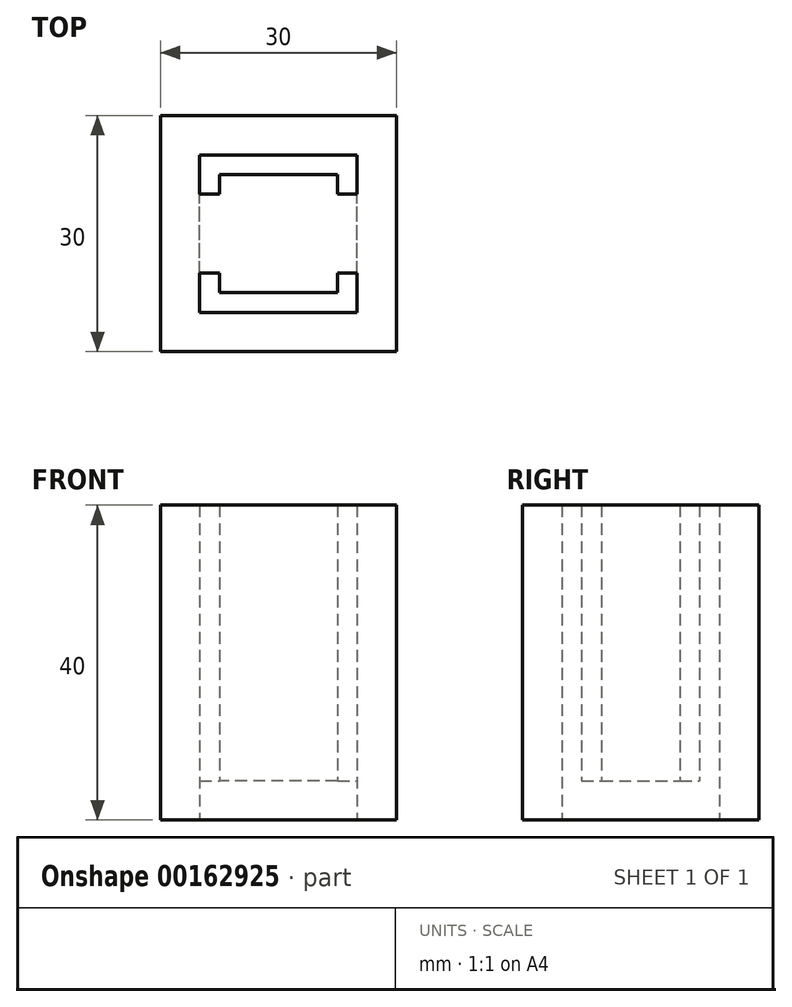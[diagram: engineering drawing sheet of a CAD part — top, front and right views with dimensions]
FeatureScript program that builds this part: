
annotation { "Feature Type Name" : "Feature", "Feature Type Description" : "" }
export const myFeature = defineFeature(function(context is Context, id is Id, definition is map)
    precondition{}
    {
        {
            var Q0;
            Q0=qCreatedBy(makeId("Top.planeOp"),FACE);
            var sketch = newSketch(context, id + "F0", { "sketchPlane" : qUnion([Q0])});
            skLineSegment(sketch, "E0.bottom", {"start": v(7.5, -7.5) * mm, "end": v(-7.5, -7.5) * mm});
            skLineSegment(sketch, "E0.top", {"start": v(7.5, 7.5) * mm, "end": v(-7.5, 7.5) * mm});
            skLineSegment(sketch, "E0.left", {"start": v(7.5, -7.5) * mm, "end": v(7.5, 7.5) * mm});
            skLineSegment(sketch, "E0.right", {"start": v(-7.5, -7.5) * mm, "end": v(-7.5, 7.5) * mm});
            skPoint(sketch, "E0.middle", {"position": v(0, 0) * mm});
            skLineSegment(sketch, "E1.bottom", {"start": v(10, -10) * mm, "end": v(-10, -10) * mm});
            skLineSegment(sketch, "E1.top", {"start": v(10, 10) * mm, "end": v(-10, 10) * mm});
            skLineSegment(sketch, "E1.left", {"start": v(10, -10) * mm, "end": v(10, 10) * mm});
            skLineSegment(sketch, "E1.right", {"start": v(-10, -10) * mm, "end": v(-10, 10) * mm});
            skLineSegment(sketch, "E2.bottom", {"start": v(-15, 15) * mm, "end": v(15, 15) * mm});
            skLineSegment(sketch, "E2.top", {"start": v(-15, -15) * mm, "end": v(15, -15) * mm});
            skLineSegment(sketch, "E2.left", {"start": v(-15, 15) * mm, "end": v(-15, -15) * mm});
            skLineSegment(sketch, "E2.right", {"start": v(15, 15) * mm, "end": v(15, -15) * mm});
            skLineSegment(sketch, "E3", {"start": v(-10, 5) * mm, "end": v(10, 5) * mm});
            skLineSegment(sketch, "E4", {"start": v(-7.5, 0) * mm, "end": v(7.5, 0) * mm, "construction": true});
            skLineSegment(sketch, "E5.MirrorCS", {"start": v(-10, -5) * mm, "end": v(10, -5) * mm});
            skSolve(sketch);
        }
        {
            var Q0;
            {var subQ0=sQuery(id+"F0.wireOp",EDGE,"E0.top");Q0=makeQuery(id+"F0.imprint","IMPRINT",FACE,{"disambiguationData":[TD([[makeQuery(id+"F0.imprint","IMPRINT",EDGE,{"derivedFrom":subQ0}),1.0]])]});}
            var Q1;
            {var subQ0=sQuery(id+"F0.wireOp",EDGE,"E5.MirrorCS");var subQ1=sQuery(id+"F0.wireOp",EDGE,"E0.left");var subQ2=makeQuery(id+"F0.imprint","INTERSECT",VERTEX,{"derivedFrom":[subQ1,subQ0]});Q1=makeQuery(id+"F0.imprint","IMPRINT",FACE,{"disambiguationData":[TD([[makeQuery(id+"F0.imprint","IMPRINT",EDGE,{"disambiguationData":[TD([[subQ2,-1.0]])],"derivedFrom":subQ1}),1.0]])]});}
            var Q2;
            {var subQ0=sQuery(id+"F0.wireOp",EDGE,"E0.bottom");Q2=makeQuery(id+"F0.imprint","IMPRINT",FACE,{"disambiguationData":[TD([[makeQuery(id+"F0.imprint","IMPRINT",EDGE,{"derivedFrom":subQ0}),-1.0]])]});}
            var Q3;
            {var subQ0=sQuery(id+"F0.wireOp",EDGE,"E5.MirrorCS");var subQ1=sQuery(id+"F0.wireOp",EDGE,"E0.left");var subQ2=makeQuery(id+"F0.imprint","INTERSECT",VERTEX,{"derivedFrom":[subQ1,subQ0]});Q3=makeQuery(id+"F0.imprint","IMPRINT",FACE,{"disambiguationData":[TD([[makeQuery(id+"F0.imprint","IMPRINT",EDGE,{"disambiguationData":[TD([[subQ2,-1.0]])],"derivedFrom":subQ1}),-1.0]])]});}
            var Q4;
            {var subQ7=sQuery(id+"F0.wireOp",EDGE,"E0.top");Q4=makeQuery(id+"F0.imprint","IMPRINT",FACE,{"disambiguationData":[TD([[makeQuery(id+"F0.imprint","IMPRINT",EDGE,{"derivedFrom":subQ7}),-1.0]])]});}
            var Q5;
            {var subQ0=sQuery(id+"F0.wireOp",EDGE,"E5.MirrorCS");var subQ1=sQuery(id+"F0.wireOp",EDGE,"E0.right");var subQ2=makeQuery(id+"F0.imprint","INTERSECT",VERTEX,{"derivedFrom":[subQ1,subQ0]});Q5=makeQuery(id+"F0.imprint","IMPRINT",FACE,{"disambiguationData":[TD([[makeQuery(id+"F0.imprint","IMPRINT",EDGE,{"disambiguationData":[TD([[subQ2,-1.0]])],"derivedFrom":subQ1}),1.0]])]});}
            var Q6;
            {var subQ2=sQuery(id+"F0.wireOp",EDGE,"E0.bottom");Q6=makeQuery(id+"F0.imprint","IMPRINT",FACE,{"disambiguationData":[TD([[makeQuery(id+"F0.imprint","IMPRINT",EDGE,{"derivedFrom":subQ2}),1.0]])]});}
            var Q7;
            {var subQ4=sQuery(id+"F0.wireOp",EDGE,"E1.bottom");Q7=makeQuery(id+"F0.imprint","IMPRINT",FACE,{"disambiguationData":[TD([[makeQuery(id+"F0.imprint","IMPRINT",EDGE,{"derivedFrom":subQ4}),1.0]])]});}
            var Q8;
            Q8=makeQuery(id+"F2.opExtrude","SWEPT_BODY",BODY,{"disambiguationData":[OSD([sQuery(id+"F0.wireOp",EDGE,"E0.bottom"),sQuery(id+"F0.wireOp",EDGE,"E0.top"),sQuery(id+"F0.wireOp",EDGE,"E0.left"),sQuery(id+"F0.wireOp",EDGE,"E0.right"),sQuery(id+"F0.wireOp",EDGE,"E1.left"),sQuery(id+"F0.wireOp",EDGE,"SQ9eBi6W-tF5L-iBfu-zbn4-8iLzbDoy28uW"),sQuery(id+"F0.wireOp",EDGE,"c3725698-1aea-4c50-8bbd-dbaeecdf150d0.MirrorCS")])]});
            extrude(context, id + "F1", {"entities" : qUnion([Q0, Q1, Q2, Q3, Q4, Q5, Q6, Q7]), "endBoundEntityBody" : qUnion([Q8]), "depth" : 40 * mm});
        }
        {
            var Q0;
            {var subQ0=sQuery(id+"F0.wireOp",EDGE,"E0.bottom");Q0=makeQuery(id+"F0.imprint","IMPRINT",FACE,{"disambiguationData":[TD([[makeQuery(id+"F0.imprint","IMPRINT",EDGE,{"derivedFrom":subQ0}),-1.0]])]});}
            var Q1;
            {var subQ0=sQuery(id+"F0.wireOp",EDGE,"E5.MirrorCS");var subQ1=sQuery(id+"F0.wireOp",EDGE,"E0.left");var subQ2=makeQuery(id+"F0.imprint","INTERSECT",VERTEX,{"derivedFrom":[subQ1,subQ0]});Q1=makeQuery(id+"F0.imprint","IMPRINT",FACE,{"disambiguationData":[TD([[makeQuery(id+"F0.imprint","IMPRINT",EDGE,{"disambiguationData":[TD([[subQ2,-1.0]])],"derivedFrom":subQ1}),1.0]])]});}
            var Q2;
            {var subQ0=sQuery(id+"F0.wireOp",EDGE,"E0.top");Q2=makeQuery(id+"F0.imprint","IMPRINT",FACE,{"disambiguationData":[TD([[makeQuery(id+"F0.imprint","IMPRINT",EDGE,{"derivedFrom":subQ0}),1.0]])]});}
            var Q3;
            {var subQ0=sQuery(id+"F0.wireOp",EDGE,"E5.MirrorCS");var subQ1=sQuery(id+"F0.wireOp",EDGE,"E0.left");var subQ2=makeQuery(id+"F0.imprint","INTERSECT",VERTEX,{"derivedFrom":[subQ1,subQ0]});Q3=makeQuery(id+"F0.imprint","IMPRINT",FACE,{"disambiguationData":[TD([[makeQuery(id+"F0.imprint","IMPRINT",EDGE,{"disambiguationData":[TD([[subQ2,-1.0]])],"derivedFrom":subQ1}),-1.0]])]});}
            var Q4;
            {var subQ0=sQuery(id+"F0.wireOp",EDGE,"E5.MirrorCS");var subQ1=sQuery(id+"F0.wireOp",EDGE,"E0.right");var subQ2=makeQuery(id+"F0.imprint","INTERSECT",VERTEX,{"derivedFrom":[subQ1,subQ0]});Q4=makeQuery(id+"F0.imprint","IMPRINT",FACE,{"disambiguationData":[TD([[makeQuery(id+"F0.imprint","IMPRINT",EDGE,{"disambiguationData":[TD([[subQ2,-1.0]])],"derivedFrom":subQ1}),1.0]])]});}
            extrude(context, id + "F2", {"entities" : qUnion([Q0, Q1, Q2, Q3, Q4]), "operationType" : NewBodyOperationType.REMOVE, "depth" : 5 * mm});
        }
        {
            var Q0;
            {var subQ2=sQuery(id+"F0.wireOp",EDGE,"E0.bottom");Q0=makeQuery(id+"F0.imprint","IMPRINT",FACE,{"disambiguationData":[TD([[makeQuery(id+"F0.imprint","IMPRINT",EDGE,{"derivedFrom":subQ2}),1.0]])]});}
            var Q1;
            {var subQ7=sQuery(id+"F0.wireOp",EDGE,"E0.top");Q1=makeQuery(id+"F0.imprint","IMPRINT",FACE,{"disambiguationData":[TD([[makeQuery(id+"F0.imprint","IMPRINT",EDGE,{"derivedFrom":subQ7}),-1.0]])]});}
            extrude(context, id + "F3", {"entities" : qUnion([Q0, Q1]), "operationType" : NewBodyOperationType.REMOVE, "depth" : 40 * mm});
        }
    });
